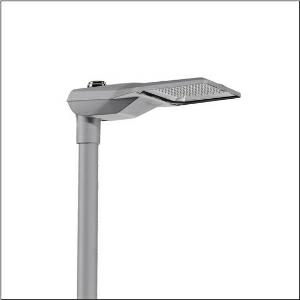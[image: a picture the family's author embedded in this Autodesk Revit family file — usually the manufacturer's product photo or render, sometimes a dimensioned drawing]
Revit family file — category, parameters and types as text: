
# Revit family: streetlight_sl_21_midi___p0_8a_5xe7u27n08mb_4af6
name_source: partatom
category: Lighting Fixtures
units: mm (PartAtom-declared; Revit-internal decimal feet)

## family parameters
Cut with Voids When Loaded = No
Host = Face
Light Source = No
Part Type = Normal
Room Calculation Point = No
Round Connector Dimension = Use Diameter
Shared = No

## types (1)
- --- (1 x LED, 15120 lm, 134.3 W, 2200K)
    Apparent Load = 134 VA
    CIE Flux Codes = 33 69 96 100 100
    Color Rendering = 70
    Color Temperature = 2200K
    Default Elevation = 1800 mm
    Description = Streetlight SL 21 midi, mast luminaire, primary light control with lens, of PMMA, primary optical cover: cover, of toughened safety glass, transparent, light distribution: P0.8a, light emission: direct distribution, primary light characteristic: asymmetric, installation type: side-entry, LED, 3G 2.5mm², High Power LED, rated luminous flux: 15.120lm, luminous efficacy: 113lm/W, light colour: 722, colour temperature: 2200K, control gear: NEMA (7pin), control: flexible luminous flux parameterisation, time-dependent luminous flux control, constant luminous flux control, pre-setting: linear dimming characteristic, overheat protection, mains connection: 220..240V, AC, 50/60Hz, connection cable pre-assembled, cable length: 12,5m, wiring characteristics: H05VV-F, start of lifetime: 134W, end of service life: 141W, reduction: 60W, luminaire housing, of diecast aluminium (EN AC-44300), powder-coated, Siteco® metallic grey (DB 702S), corrosivity category C5 mid according to DIN EN ISO 12944, multi-level sealing system, sealing non-destructively replaceable, inclination adjustable: 0°, 5°, 10°, 15°, length: 644mm, width: 335mm, height: 110mm, spigot size: 42mm (side-entry), mounting height: 4..8m, protection rating (complete): IP66, insulation class (complete): insulation class I (protective earthing), certification: CE, ENEC, ENEC+, VDE, impact resistance: IK10, permissible operating ambient temperature for outdoor applications: -40..+50°C, standard-compliant lighting for roads and squares, packaging unit: 1 piece

Light Distribution: P0.8a
    Height = 111 mm
    Lamp = 1 x LED
    Lamp Light Flux = 15120 lm
    Lamp Power = 134.3 W
    Lamp count = 1
    Length = 644 mm
    Luminous efficacy = 113 lm/W
    Manufacturer = Siteco
    ModVariant = No
    Model = 5XE7U27N08MB
    Number of Poles = 1
    OnlyDefault = Yes
    Power Factor = 1
    Product Name = Streetlight SL 21 midi | P0.8a
    Product group = mast luminaire | pylon top
    ProductGroupID = 6100
    Protection Class = Protection class I
    Protection Degree = IP 66
    RLX_Detail_Level = 1
    RLX_Emergency_Light_Flux = 0 lm
    RLX_Emergency_Type = 0
    RLX_Emergency_Type_DB = No
    RlxData = <blob elided: 89797 chars, md5=2c32ab07>
    Socket = socket
    Standby Power = 0 W
    System Light Flux = 15119 lm
    System Power = 134 W
    Type Comments = factory setting: luminous flux: 100 % | dim-lin: 254 | 687 mA
    Type Image = l_1294377.jpg
    URL = http://relux.com
    VarID = @adj_094831
    Voltage = 0 V
    Weight = 0.00 kg
    Width = 336 mm

## geometry (parser evidence)
native form markers: Blend x4, Sweep x10
no freeform markers — native parametric forms only
